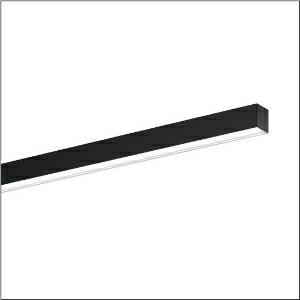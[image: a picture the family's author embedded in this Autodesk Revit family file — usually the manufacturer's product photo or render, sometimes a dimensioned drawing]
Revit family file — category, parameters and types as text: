
# Revit family: silica_r__21_51mx20db32bb_e5b9
name_source: partatom
category: Lighting Fixtures
units: mm (PartAtom-declared; Revit-internal decimal feet)

## family parameters
Cut with Voids When Loaded = No
Host = Face
Light Source = No
Part Type = Normal
Room Calculation Point = No
Round Connector Dimension = Use Diameter
Shared = No

## types (1)
- --- (1 x LED, 3000 lm, 20.2 W, 3000K)
    Apparent Load = 20 VA
    CIE Flux Codes = 48 79 96 100 100
    Color Rendering = 80
    Color Temperature = 3000K
    Default Elevation = 1800 mm
    Description = Silica® 21, office luminaire, primary optical cover: cover, of PMMA, opal, light emission: direct distribution, primary light characteristic: symmetric, installation type: surface-mounted, LED, rated luminous flux: 3.000lm, luminous efficacy: 149lm/W, light colour: 830, colour temperature: 3000K, control gear: DALI 2, with terminal, 3+2-pole, max. 2.5mm², mains connection: 220..240V, AC, 50/60Hz, luminaire housing, of aluminium, matt jet black (RAL 9005), length: 1.504mm, width: 53mm, height: 53mm, protection rating (complete): IP20, insulation class (complete): insulation class I (protective earthing), certification: CE, permissible operating ambient temperature: 0..+35°C, standard: EN 50419, packaging unit: 1 piece
    Height = 53 mm
    Lamp = 1 x LED
    Lamp Light Flux = 3000 lm
    Lamp Power = 20.2 W
    Lamp count = 1
    Length = 1504 mm
    Luminous efficacy = 149 lm/W
    Manufacturer = Siteco
    ModVariant = No
    Model = 51MX20DB32BB
    Mounting Place = Ceiling
    Mounting Type = Surface mounted
    Number of Poles = 1
    OnlyDefault = Yes
    Power Factor = 1
    Product Name = Silica® 21
    Product group = office luminaire | ceiling mounted
    ProductGroupID = 302
    Protection Class = Protection class I
    Protection Degree = IP 20
    RLX_Detail_Level = 1
    RLX_Emergency_Light_Flux = 0 lm
    RLX_Emergency_Type = 0
    RLX_Emergency_Type_DB = No
    RlxData = <blob elided: 28601 chars, md5=3173a5df>
    Socket = socket
    Standby Power = 0 W
    System Light Flux = 3000 lm
    System Power = 20 W
    Type Comments = factory setting: luminous flux: 100 % | dim-lin: 254 | 233 mA
    Type Image = l_1335925.jpg
    URL = http://relux.com
    VarID = @adj_118050
    Voltage = 0 V
    Weight = 0.00 kg
    Width = 53 mm

## geometry (parser evidence)
native form markers: Blend x4, Sweep x12
no freeform markers — native parametric forms only
